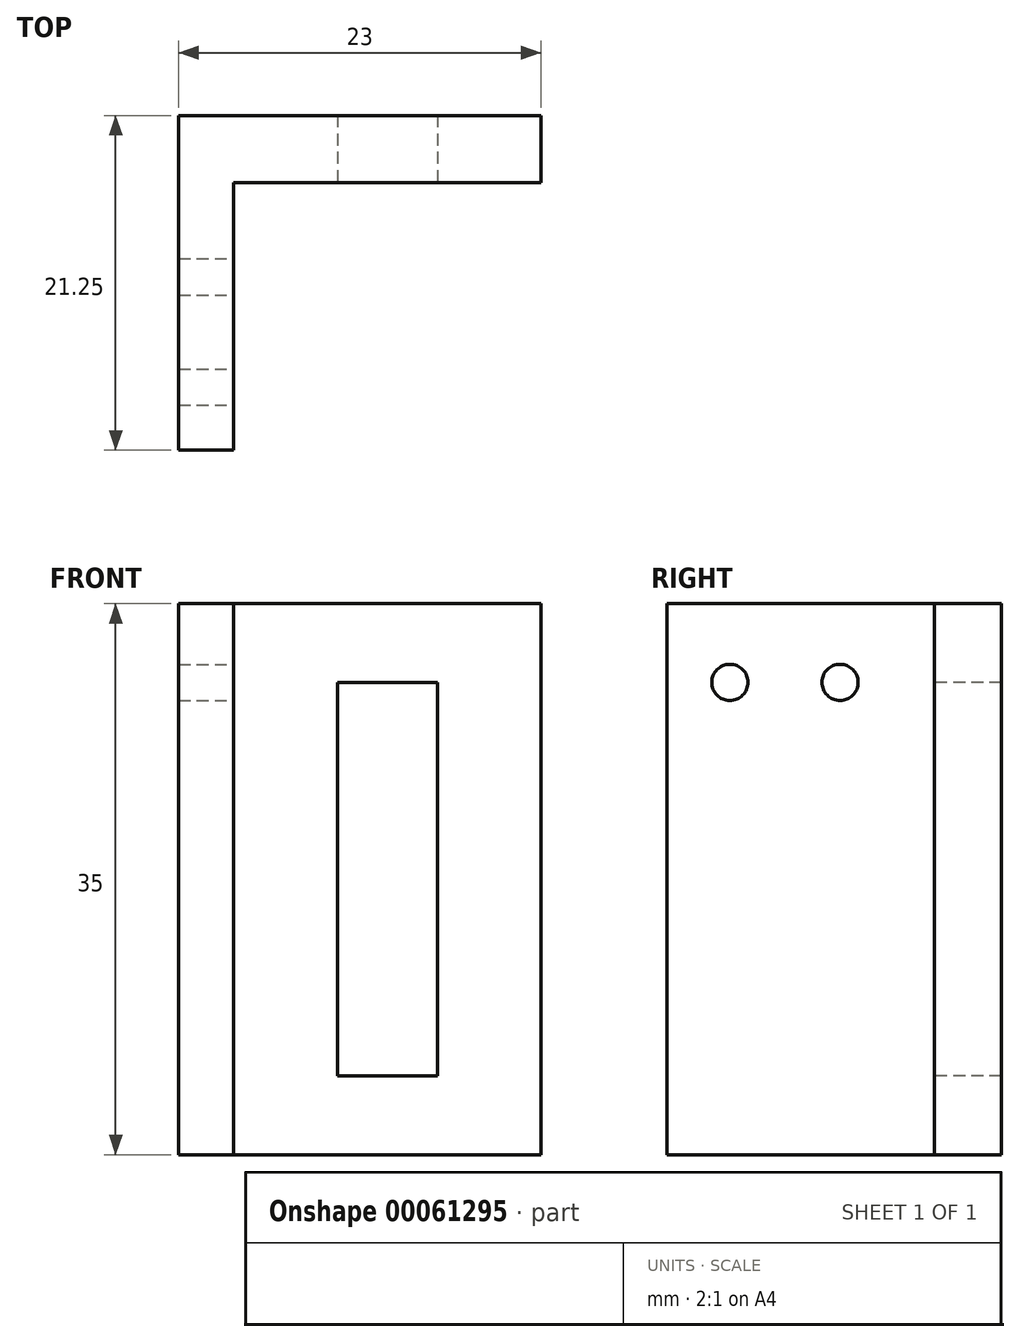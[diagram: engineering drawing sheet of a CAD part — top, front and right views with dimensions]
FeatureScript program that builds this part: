
annotation { "Feature Type Name" : "Feature", "Feature Type Description" : "" }
export const myFeature = defineFeature(function(context is Context, id is Id, definition is map)
    precondition{}
    {
        {
            var Q0;
            Q0=qCreatedBy(makeId("Front.planeOp"),FACE);
            var sketch = newSketch(context, id + "F0", { "sketchPlane" : qUnion([Q0])});
            skLineSegment(sketch, "E0.rect.bottom", {"start": v(11.57, -17.5) * mm, "end": v(-11.43, -17.5) * mm});
            skLineSegment(sketch, "E0.rect.top", {"start": v(11.57, 17.5) * mm, "end": v(-11.43, 17.5) * mm});
            skLineSegment(sketch, "E0.rect.left", {"start": v(11.57, -17.5) * mm, "end": v(11.57, 17.5) * mm});
            skLineSegment(sketch, "E0.rect.right", {"start": v(-11.43, -17.5) * mm, "end": v(-11.43, 17.5) * mm});
            skPoint(sketch, "E0.rect.middle", {"position": v(0.07, 0) * mm});
            skSolve(sketch);
        }
        {
            var Q0;
            Q0=makeQuery(id+"F0.imprint","IMPRINT",FACE,{"disambiguationData":[TD([[makeQuery(id+"F0.imprint","IMPRINT",EDGE,{"derivedFrom":sQuery(id+"F0.wireOp",EDGE,"E0.rect.bottom")}),-1.0]])]});
            extrude(context, id + "F1", {"entities" : qUnion([Q0]), "oppositeDirection" : true, "depth" : 4.25 * mm});
        }
        {
            var Q0;
            Q0=makeQuery(id+"F1.opExtrude","CAP_FACE",FACE,{"disambiguationData":[OSD([sQuery(id+"F0.wireOp",EDGE,"E0.rect.bottom"),sQuery(id+"F0.wireOp",EDGE,"E0.rect.top"),sQuery(id+"F0.wireOp",EDGE,"E0.rect.left"),sQuery(id+"F0.wireOp",EDGE,"E0.rect.right")])],"isStart":true});
            var sketch = newSketch(context, id + "F2", { "sketchPlane" : qUnion([Q0])});
            skLineSegment(sketch, "E1.bottom", {"start": v(-11.43, 17.5) * mm, "end": v(-7.93, 17.5) * mm});
            skLineSegment(sketch, "E1.top", {"start": v(-11.43, -17.5) * mm, "end": v(-7.93, -17.5) * mm});
            skLineSegment(sketch, "E1.left", {"start": v(-11.43, 17.5) * mm, "end": v(-11.43, -17.5) * mm});
            skLineSegment(sketch, "E1.right", {"start": v(-7.93, 17.5) * mm, "end": v(-7.93, -17.5) * mm});
            skSolve(sketch);
        }
        {
            var Q0;
            Q0=makeQuery(id+"F2.imprint","IMPRINT",FACE,{"disambiguationData":[TD([[makeQuery(id+"F2.imprint","IMPRINT",EDGE,{"derivedFrom":sQuery(id+"F2.wireOp",EDGE,"E1.bottom")}),1.0]])]});
            extrude(context, id + "F3", {"entities" : qUnion([Q0]), "operationType" : NewBodyOperationType.ADD, "depth" : 17 * mm});
        }
        {
            var Q0;
            Q0=makeQuery(id+"F1.opExtrude","CAP_FACE",FACE,{"disambiguationData":[OSD([sQuery(id+"F0.wireOp",EDGE,"E0.rect.bottom"),sQuery(id+"F0.wireOp",EDGE,"E0.rect.top"),sQuery(id+"F0.wireOp",EDGE,"E0.rect.left"),sQuery(id+"F0.wireOp",EDGE,"E0.rect.right")])],"isStart":true});
            var sketch = newSketch(context, id + "F4", { "sketchPlane" : qUnion([Q0])});
            skLineSegment(sketch, "E2", {"start": v(1.82, 17.5) * mm, "end": v(1.82, -17.5) * mm, "construction": true});
            skLineSegment(sketch, "E3.rect.bottom", {"start": v(5, 12.5) * mm, "end": v(-1.36, 12.5) * mm});
            skLineSegment(sketch, "E3.rect.top", {"start": v(5, -12.5) * mm, "end": v(-1.36, -12.5) * mm});
            skLineSegment(sketch, "E3.rect.left", {"start": v(5, 12.5) * mm, "end": v(5, -12.5) * mm});
            skLineSegment(sketch, "E3.rect.right", {"start": v(-1.36, 12.5) * mm, "end": v(-1.36, -12.5) * mm});
            skPoint(sketch, "E3.rect.middle", {"position": v(1.82, 0) * mm});
            skSolve(sketch);
        }
        {
            var Q0;
            Q0 = qSketchRegion(id + "F4", true);
            extrude(context, id + "F5", {"entities" : qUnion([Q0]), "operationType" : NewBodyOperationType.REMOVE, "endBound" : BoundingType.THROUGH_ALL, "oppositeDirection" : true, "depth" : 25 * mm});
        }
        {
            var Q0;
            Q0=makeQuery(id+"F3.opExtrude","SWEPT_FACE",FACE,{"disambiguationData":[OSD([sQuery(id+"F2.wireOp",EDGE,"E1.right")])]});
            var sketch = newSketch(context, id + "F6", { "sketchPlane" : qUnion([Q0])});
            skCircle(sketch, "E4", {"center": v(-13, 12.5) * mm, "radius": 1.15 * mm});
            skLineSegment(sketch, "E5.1", {"start": v(-12, -12.5) * mm, "end": v(-5, -12.5) * mm});
            skCircle(sketch, "E6", {"center": v(-6, 12.5) * mm, "radius": 1.15 * mm});
            skSolve(sketch);
        }
        {
            var Q0;
            Q0 = qSketchRegion(id + "F6", true);
            extrude(context, id + "F7", {"entities" : qUnion([Q0]), "operationType" : NewBodyOperationType.REMOVE, "endBound" : BoundingType.THROUGH_ALL, "oppositeDirection" : true, "depth" : 25 * mm});
        }
    });
